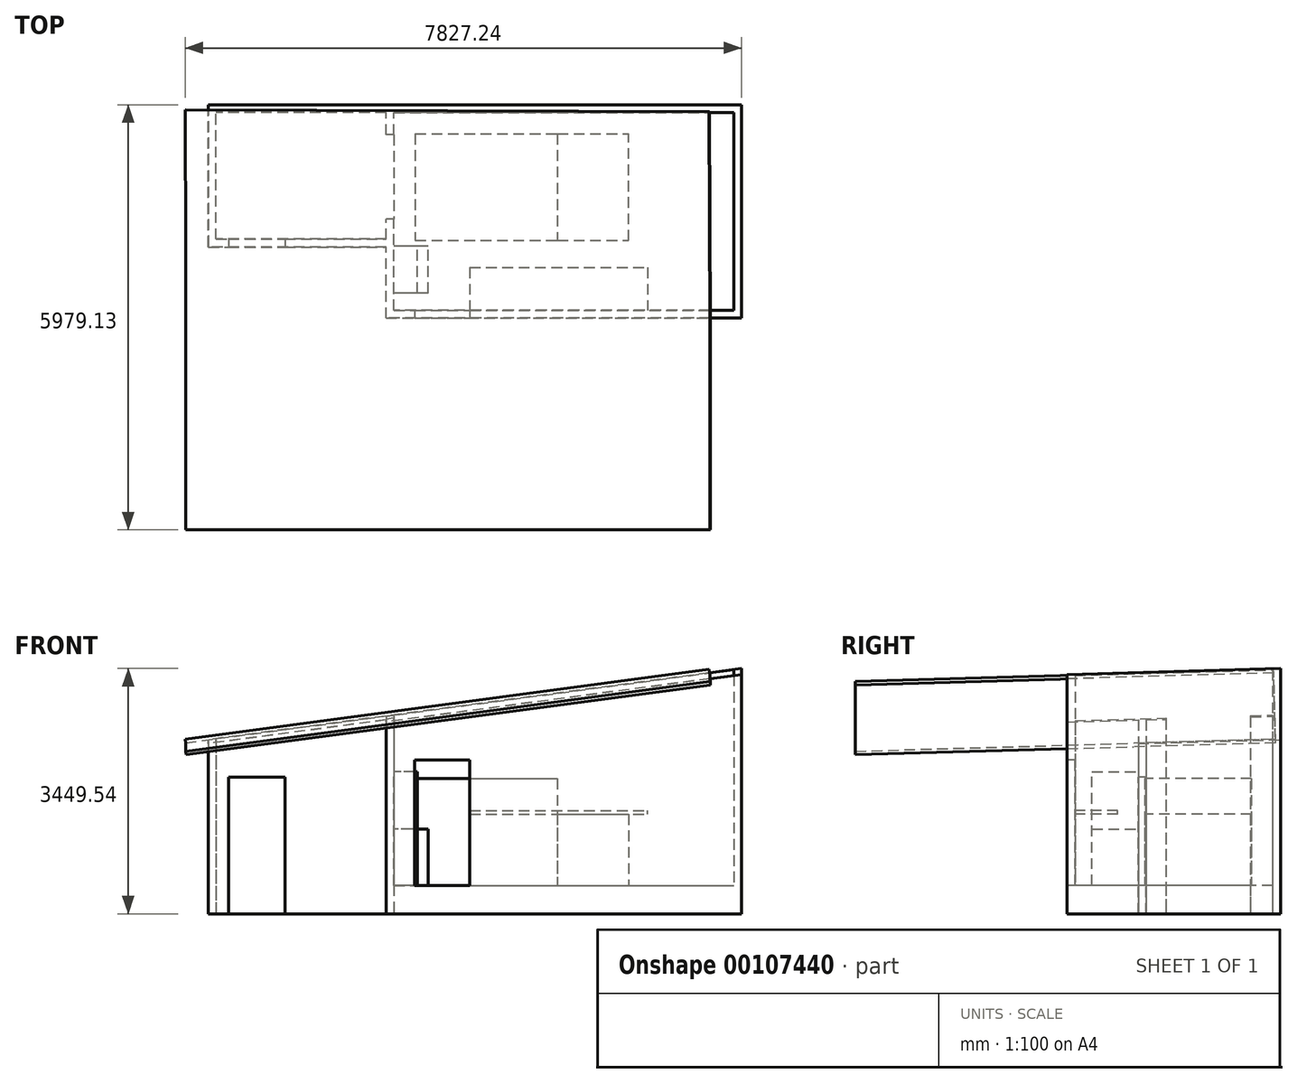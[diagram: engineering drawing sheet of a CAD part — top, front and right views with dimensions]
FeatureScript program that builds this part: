
annotation { "Feature Type Name" : "Feature", "Feature Type Description" : "" }
export const myFeature = defineFeature(function(context is Context, id is Id, definition is map)
    precondition{}
    {
        {
            var Q0;
            Q0=qCreatedBy(makeId("Top.planeOp"),FACE);
            var sketch = newSketch(context, id + "F0", { "sketchPlane" : qUnion([Q0])});
            skLineSegment(sketch, "E0.bottom", {"start": v(-63.87, 1825.98) * mm, "end": v(2436.13, 1825.98) * mm});
            skLineSegment(sketch, "E0.top", {"start": v(-63.87, -174.02) * mm, "end": v(2436.13, -174.02) * mm});
            skLineSegment(sketch, "E0.left", {"start": v(-63.87, 1825.98) * mm, "end": v(-63.87, -174.02) * mm});
            skLineSegment(sketch, "E0.right", {"start": v(2436.13, 1825.98) * mm, "end": v(2436.13, -174.02) * mm});
            skLineSegment(sketch, "E1.bottom", {"start": v(2436.13, 1825.98) * mm, "end": v(7436.13, 1825.98) * mm});
            skLineSegment(sketch, "E1.top", {"start": v(2436.13, -1174.02) * mm, "end": v(7436.13, -1174.02) * mm});
            skLineSegment(sketch, "E1.left", {"start": v(2436.13, 1825.98) * mm, "end": v(2436.13, -1174.02) * mm});
            skLineSegment(sketch, "E1.right", {"start": v(7436.13, 1825.98) * mm, "end": v(7436.13, -1174.02) * mm});
            skLineSegment(sketch, "E2.0", {"start": v(2546.13, 1715.98) * mm, "end": v(7326.13, 1715.98) * mm});
            skLineSegment(sketch, "E2.1", {"start": v(2546.13, 1715.98) * mm, "end": v(2546.13, -1064.02) * mm});
            skLineSegment(sketch, "E2.2", {"start": v(2546.13, -1064.02) * mm, "end": v(7326.13, -1064.02) * mm});
            skLineSegment(sketch, "E2.3", {"start": v(7326.13, 1715.98) * mm, "end": v(7326.13, -1064.02) * mm});
            skLineSegment(sketch, "E3.1", {"start": v(46.13, 1715.98) * mm, "end": v(46.13, -64.02) * mm});
            skLineSegment(sketch, "E3.2", {"start": v(46.13, -64.02) * mm, "end": v(2436.13, -64.02) * mm});
            skLineSegment(sketch, "E4", {"start": v(46.13, 1715.98) * mm, "end": v(2436.13, 1715.98) * mm});
            skLineSegment(sketch, "E5", {"start": v(2436.13, 1404.02) * mm, "end": v(2546.13, 1404.02) * mm});
            skLineSegment(sketch, "E6", {"start": v(2436.13, 217.77) * mm, "end": v(2546.13, 217.77) * mm});
            skSolve(sketch);
        }
        {
            var Q0;
            Q0=sQuery(id+"F0.wireOp",EDGE,"E0.bottom");
            var Q1;
            Q1=sQuery(id+"F0.wireOp",VERTEX,"E0.left.start");
            cPlane(context, id + "F1", {"entities" : qUnion([Q0, Q1]), "cplaneType" : CPlaneType.LINE_POINT, "offset" : 2500 * mm, "width" : 150 * mm, "height" : 150 * mm});
        }
        {
            var Q0;
            Q0=qCreatedBy(id+"F1.planeOp",FACE);
            var sketch = newSketch(context, id + "F2", { "sketchPlane" : qUnion([Q0])});
            skLineSegment(sketch, "E7", {"start": v(1825.98, 0) * mm, "end": v(1825.98, 2500) * mm, "construction": true});
            skLineSegment(sketch, "E8", {"start": v(74.59, 0) * mm, "end": v(74.59, 2449.78) * mm, "construction": true});
            skSolve(sketch);
        }
        {
            var Q0;
            Q0=sQuery(id+"F0.wireOp",EDGE,"E1.bottom");
            var Q1;
            Q1=sQuery(id+"F0.wireOp",VERTEX,"E1.bottom.end");
            cPlane(context, id + "F3", {"entities" : qUnion([Q0, Q1]), "cplaneType" : CPlaneType.LINE_POINT, "offset" : 25 * mm, "width" : 150 * mm, "height" : 150 * mm});
        }
        {
            var Q0;
            Q0=qCreatedBy(id+"F3.planeOp",FACE);
            var sketch = newSketch(context, id + "F4", { "sketchPlane" : qUnion([Q0])});
            skLineSegment(sketch, "E9", {"start": v(1825.98, 0) * mm, "end": v(1825.98, 3500) * mm, "construction": true});
            skSolve(sketch);
        }
        {
            var Q0;
            Q0=sQuery(id+"F2.wireOp",VERTEX,"E7.end");
            var Q1;
            Q1=sQuery(id+"F2.wireOp",VERTEX,"E8.end");
            var Q2;
            Q2=sQuery(id+"F4.wireOp",VERTEX,"E9.end");
            cPlane(context, id + "F5", {"entities" : qUnion([Q0, Q1, Q2]), "cplaneType" : CPlaneType.THREE_POINT, "offset" : 25 * mm, "width" : 150 * mm, "height" : 150 * mm});
        }
        {
            var Q0;
            Q0=qCreatedBy(id+"F5.planeOp",FACE);
            var sketch = newSketch(context, id + "F6", { "sketchPlane" : qUnion([Q0])});
            skLineSegment(sketch, "E10.0", {"start": v(-70.22, -1825.23) * mm, "end": v(-62.65, 173.95) * mm});
            skLineSegment(sketch, "E11.0", {"start": v(-70.22, -1825.23) * mm, "end": v(2407.87, -1825.23) * mm});
            skLineSegment(sketch, "E12.0", {"start": v(2407.87, -1825.23) * mm, "end": v(7364.04, -1825.23) * mm});
            skLineSegment(sketch, "E13.0", {"start": v(7364.04, -1825.23) * mm, "end": v(7375.4, 1173.54) * mm});
            skLineSegment(sketch, "E14", {"start": v(7375.4, 1173.54) * mm, "end": v(7375.4, 4057.76) * mm});
            skLineSegment(sketch, "E15", {"start": v(7375.4, 4057.76) * mm, "end": v(-62.65, 4085.93) * mm});
            skLineSegment(sketch, "E16", {"start": v(-62.65, 4085.93) * mm, "end": v(-62.65, 173.95) * mm});
            skPoint(sketch, "E17.0", {"position": v(7826.24, -1925.54) * mm});
            skLineSegment(sketch, "E18", {"start": v(7364.04, -1825.23) * mm, "end": v(7826.24, -1925.54) * mm});
            skSolve(sketch);
        }
        {
            var Q0;
            Q0=makeQuery(id+"F6.imprint","IMPRINT",FACE,{"disambiguationData":[TD([[makeQuery(id+"F6.imprint","IMPRINT",EDGE,{"derivedFrom":sQuery(id+"F6.wireOp",EDGE,"E10.0")}),-1.0]])]});
            extrude(context, id + "F7", {"entities" : qUnion([Q0]), "depth" : 50 * mm});
        }
        {
            var Q0;
            {var subQ4=sQuery(id+"F0.wireOp",EDGE,"E1.bottom");Q0=makeQuery(id+"F0.imprint","IMPRINT",FACE,{"disambiguationData":[TD([[makeQuery(id+"F0.imprint","IMPRINT",EDGE,{"derivedFrom":subQ4}),-1.0]])]});}
            var Q1;
            {var subQ1=sQuery(id+"F0.wireOp",EDGE,"E0.bottom");Q1=makeQuery(id+"F0.imprint","IMPRINT",FACE,{"disambiguationData":[TD([[makeQuery(id+"F0.imprint","IMPRINT",EDGE,{"derivedFrom":subQ1}),-1.0]])]});}
            var Q2;
            {var subQ0=sQuery(id+"F0.wireOp",EDGE,"E3.0");var subQ1=sQuery(id+"F0.wireOp",EDGE,"E1.left");var subQ2=makeQuery(id+"F0.imprint","INTERSECT",VERTEX,{"derivedFrom":[subQ1,subQ0]});Q2=makeQuery(id+"F0.imprint","IMPRINT",FACE,{"disambiguationData":[TD([[makeQuery(id+"F0.imprint","IMPRINT",EDGE,{"disambiguationData":[TD([[subQ2,-1.0]])],"derivedFrom":subQ1}),1.0]])]});}
            var Q3;
            Q3=makeQuery(id+"F7.opExtrude","CAP_FACE",FACE,{"disambiguationData":[OSD([sQuery(id+"F6.wireOp",EDGE,"E10.0"),sQuery(id+"F6.wireOp",EDGE,"E11.0"),sQuery(id+"F6.wireOp",EDGE,"E12.0"),sQuery(id+"F6.wireOp",EDGE,"E13.0"),sQuery(id+"F6.wireOp",EDGE,"E14"),sQuery(id+"F6.wireOp",EDGE,"E15"),sQuery(id+"F6.wireOp",EDGE,"E16")])],"isStart":false});
            extrude(context, id + "F8", {"entities" : qUnion([Q0, Q1, Q2]), "endBound" : BoundingType.UP_TO_SURFACE, "endBoundEntityFace" : qUnion([Q3]), "depth" : 25 * mm});
        }
        {
            var Q0;
            Q0=makeQuery(id+"F8.opExtrude","SWEPT_FACE",FACE,{"disambiguationData":[OSD([sQuery(id+"F0.wireOp",EDGE,"E0.top")])]});
            var sketch = newSketch(context, id + "F9", { "sketchPlane" : qUnion([Q0])});
            skLineSegment(sketch, "E19.bottom", {"start": v(219.42, 0) * mm, "end": v(1012.37, 0) * mm});
            skLineSegment(sketch, "E19.top", {"start": v(219.42, 1923.74) * mm, "end": v(1012.37, 1923.74) * mm});
            skLineSegment(sketch, "E19.left", {"start": v(219.42, 0) * mm, "end": v(219.42, 1923.74) * mm});
            skLineSegment(sketch, "E19.right", {"start": v(1012.37, 0) * mm, "end": v(1012.37, 1923.74) * mm});
            skSolve(sketch);
        }
        {
            var Q0;
            Q0=makeQuery(id+"F9.imprint","IMPRINT",FACE,{"disambiguationData":[TD([[makeQuery(id+"F9.imprint","IMPRINT",EDGE,{"derivedFrom":sQuery(id+"F9.wireOp",EDGE,"E19.bottom")}),1.0]])]});
            extrude(context, id + "F10", {"entities" : qUnion([Q0]), "operationType" : NewBodyOperationType.REMOVE, "endBound" : BoundingType.UP_TO_NEXT, "oppositeDirection" : true, "depth" : 25 * mm});
        }
        {
            var Q0;
            Q0=makeQuery(id+"F8.opExtrude","SWEPT_FACE",FACE,{"disambiguationData":[OSD([sQuery(id+"F0.wireOp",EDGE,"E1.top")])]});
            var sketch = newSketch(context, id + "F11", { "sketchPlane" : qUnion([Q0])});
            skLineSegment(sketch, "E20.bottom", {"start": v(2837.74, 394.93) * mm, "end": v(3611.42, 394.93) * mm});
            skLineSegment(sketch, "E20.top", {"start": v(2837.74, 2164) * mm, "end": v(3611.42, 2164) * mm});
            skLineSegment(sketch, "E20.left", {"start": v(2837.74, 394.93) * mm, "end": v(2837.74, 2164) * mm});
            skLineSegment(sketch, "E20.right", {"start": v(3611.42, 394.93) * mm, "end": v(3611.42, 2164) * mm});
            skSolve(sketch);
        }
        {
            var Q0;
            Q0=makeQuery(id+"F11.imprint","IMPRINT",FACE,{"disambiguationData":[TD([[makeQuery(id+"F11.imprint","IMPRINT",EDGE,{"derivedFrom":sQuery(id+"F11.wireOp",EDGE,"E20.bottom")}),1.0]])]});
            extrude(context, id + "F12", {"entities" : qUnion([Q0]), "operationType" : NewBodyOperationType.REMOVE, "endBound" : BoundingType.UP_TO_NEXT, "oppositeDirection" : true, "depth" : 25 * mm});
        }
        {
            var Q0;
            {var subQ2=sQuery(id+"F0.wireOp",EDGE,"E2.0");Q0=makeQuery(id+"F0.imprint","IMPRINT",FACE,{"disambiguationData":[TD([[makeQuery(id+"F0.imprint","IMPRINT",EDGE,{"derivedFrom":subQ2}),-1.0]])]});}
            extrude(context, id + "F13", {"entities" : qUnion([Q0]), "operationType" : NewBodyOperationType.ADD, "depth" : 400 * mm});
        }
        {
            var Q0;
            {var subQ0=sQuery(id+"F0.wireOp",EDGE,"E2.1");Q0=makeQuery(id+"F8.opExtrude","SWEPT_FACE",FACE,{"disambiguationData":[OSD([subQ0]),TDD([makeQuery(id+"F0.imprint","IMPRINT",EDGE,{"disambiguationData":[TD([[makeQuery(id+"F0.imprint","INTERSECT",VERTEX,{"derivedFrom":[subQ0,sQuery(id+"F0.wireOp",EDGE,"E2.2")]}),1.0]])],"derivedFrom":subQ0})])]});}
            var sketch = newSketch(context, id + "F14", { "sketchPlane" : qUnion([Q0])});
            skLineSegment(sketch, "E21.bottom", {"start": v(-824.02, 400) * mm, "end": v(-164.02, 400) * mm});
            skLineSegment(sketch, "E21.top", {"start": v(-824.02, 1190) * mm, "end": v(-164.02, 1190) * mm});
            skLineSegment(sketch, "E21.left", {"start": v(-824.02, 400) * mm, "end": v(-824.02, 1190) * mm});
            skLineSegment(sketch, "E21.right", {"start": v(-164.02, 400) * mm, "end": v(-164.02, 1190) * mm});
            skLineSegment(sketch, "E22.top", {"start": v(-824.02, 2000) * mm, "end": v(-164.02, 2000) * mm});
            skLineSegment(sketch, "E22.left", {"start": v(-824.02, 1190) * mm, "end": v(-824.02, 2000) * mm});
            skLineSegment(sketch, "E22.right", {"start": v(-164.02, 1190) * mm, "end": v(-164.02, 2000) * mm});
            skSolve(sketch);
        }
        {
            var Q0;
            Q0=makeQuery(id+"F14.imprint","IMPRINT",FACE,{"disambiguationData":[TD([[makeQuery(id+"F14.imprint","IMPRINT",EDGE,{"derivedFrom":sQuery(id+"F14.wireOp",EDGE,"E21.bottom")}),-1.0]])]});
            extrude(context, id + "F15", {"entities" : qUnion([Q0]), "depth" : 480 * mm});
        }
        {
            var Q0;
            Q0 = qSketchRegion(id + "F14", true);
            extrude(context, id + "F16", {"entities" : qUnion([Q0]), "depth" : 330 * mm});
        }
        {
            var Q0;
            Q0=makeQuery(id+"F13.opExtrude","CAP_FACE",FACE,{"disambiguationData":[OSD([sQuery(id+"F0.wireOp",EDGE,"E2.0"),sQuery(id+"F0.wireOp",EDGE,"E2.1"),sQuery(id+"F0.wireOp",EDGE,"E2.2"),sQuery(id+"F0.wireOp",EDGE,"E2.3")])],"isStart":false});
            var sketch = newSketch(context, id + "F17", { "sketchPlane" : qUnion([Q0])});
            skLineSegment(sketch, "E23.bottom", {"start": v(2846.13, 1415.98) * mm, "end": v(4846.13, 1415.98) * mm});
            skLineSegment(sketch, "E23.top", {"start": v(2846.13, -84.02) * mm, "end": v(4846.13, -84.02) * mm});
            skLineSegment(sketch, "E23.left", {"start": v(2846.13, 1415.98) * mm, "end": v(2846.13, -84.02) * mm});
            skLineSegment(sketch, "E23.right", {"start": v(4846.13, 1415.98) * mm, "end": v(4846.13, -84.02) * mm});
            skPoint(sketch, "E24.oppositeSnap0", {"position": v(3846.13, 1415.98) * mm});
            skLineSegment(sketch, "E24.bottom", {"start": v(4846.13, -84.02) * mm, "end": v(5846.13, -84.02) * mm});
            skLineSegment(sketch, "E24.top", {"start": v(4846.13, 1415.98) * mm, "end": v(5846.13, 1415.98) * mm});
            skLineSegment(sketch, "E24.left", {"start": v(4846.13, -84.02) * mm, "end": v(4846.13, 1415.98) * mm});
            skLineSegment(sketch, "E24.right", {"start": v(5846.13, -84.02) * mm, "end": v(5846.13, 1415.98) * mm});
            skSolve(sketch);
        }
        {
            var Q0;
            Q0=makeQuery(id+"F17.imprint","IMPRINT",FACE,{"disambiguationData":[TD([[makeQuery(id+"F17.imprint","IMPRINT",EDGE,{"derivedFrom":sQuery(id+"F17.wireOp",EDGE,"E23.bottom")}),-1.0]])]});
            extrude(context, id + "F18", {"entities" : qUnion([Q0]), "depth" : 1500 * mm});
        }
        {
            var Q0;
            Q0=makeQuery(id+"F17.imprint","IMPRINT",FACE,{"disambiguationData":[TD([[makeQuery(id+"F17.imprint","IMPRINT",EDGE,{"derivedFrom":sQuery(id+"F17.wireOp",EDGE,"E24.bottom")}),1.0]])]});
            extrude(context, id + "F19", {"entities" : qUnion([Q0]), "depth" : 1000 * mm});
        }
        {
            var Q0;
            Q0=makeQuery(id+"F8.opExtrude","SWEPT_FACE",FACE,{"disambiguationData":[OSD([sQuery(id+"F0.wireOp",EDGE,"E2.2")])]});
            var sketch = newSketch(context, id + "F20", { "sketchPlane" : qUnion([Q0])});
            skLineSegment(sketch, "E25.bottom", {"start": v(-3611.42, 1400) * mm, "end": v(-6111.42, 1400) * mm});
            skLineSegment(sketch, "E25.top", {"start": v(-3611.42, 1450) * mm, "end": v(-6111.42, 1450) * mm});
            skLineSegment(sketch, "E25.left", {"start": v(-3611.42, 1400) * mm, "end": v(-3611.42, 1450) * mm});
            skLineSegment(sketch, "E25.right", {"start": v(-6111.42, 1400) * mm, "end": v(-6111.42, 1450) * mm});
            skSolve(sketch);
        }
        {
            var Q0;
            Q0=makeQuery(id+"F20.imprint","IMPRINT",FACE,{"disambiguationData":[TD([[makeQuery(id+"F20.imprint","IMPRINT",EDGE,{"derivedFrom":sQuery(id+"F20.wireOp",EDGE,"E25.bottom")}),-1.0]])]});
            extrude(context, id + "F21", {"entities" : qUnion([Q0]), "depth" : 600 * mm});
        }
    });
